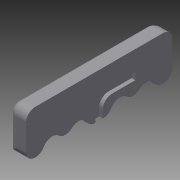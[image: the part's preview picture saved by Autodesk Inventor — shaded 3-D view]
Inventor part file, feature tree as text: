
AUTODESK INVENTOR PART (.ipt)
format: ipt  version: 2015 (Build 190159000, 159)  size: 235,520 bytes
history: native  units: in
note: dims shown in document units (in); Inventor stores cm internally (conversion verified against a paired STEP export)
features: extrude x3, sketch x3, projected_geometry x2, fillet x1, other x1
ambient origin geometry x8: Origin, YZ Plane, XZ Plane, XY Plane, X Axis, Y Axis, Z Axis, Center Point
bodies: Solid1 (feature_tree)
feature tree (10):
  extrude  "Extrusion1"  Depth=2.0in
  extrude  "Extrusion2"  Depth=0.1in
  fillet  "Fillet1"  Radius=0.125in
  other  "Lip1"
  extrude  "Extrusion3"  Depth=0.125in
  sketch  "Sketch1"  dims[d0=0.6in d1=2.0in]
  sketch  "Sketch2"  dims[d2=0.25in d3=0.0in d4=0.1in d5=0.125in]
  projected_geometry  "Projected Loop1"
  sketch  "Sketch3"  dims[d6=0.05in d7=0.0in d8=0.125in d9=0.03in d10=0.03in d11=0.0in d12=0.0in d13=0.0in d14=0.0in d15=0.125in d16=0.125in d17=0.25in d18=0.25in d19=0.05in d20=0.0in]
  projected_geometry  "Projected Loop2"
